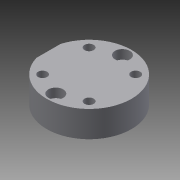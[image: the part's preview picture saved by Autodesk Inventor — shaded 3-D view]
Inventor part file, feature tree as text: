
AUTODESK INVENTOR PART (.ipt)
format: ipt  version: 2014 SP2 (Build 180246200, 246)  size: 247,296 bytes
history: native  units: in
note: dims shown in document units (in); Inventor stores cm internally (conversion verified against a paired STEP export)
features: other x259, sketch x7, hole x4, revolve x2, extrude x1, thread x1, pattern_linear x1
ambient origin geometry x8: Origin, YZ Plane, XZ Plane, XY Plane, X Axis, Y Axis, Z Axis, Center Point
bodies: Solid1 (feature_tree)
feature tree (275):
  revolve  "Revolution1"  [1 undecoded]
  extrude  "Extrusion1"  Depth=0.1831in TaperAngle=0.0deg
  revolve  "Revolution2"  [1 undecoded]
  thread  "Thread1"  [1 undecoded]
  hole  "Hole1"  [1 undecoded]
  hole  "Hole2"  [1 undecoded]
  hole  "Hole3"  [1 undecoded]
  hole  "Hole4"  [1 undecoded]
  pattern_linear  "Rectangular Pattern1"  [2 undecoded]
  other  "a1_XY"
  other  "a1_YZ"
  other  "a1_ZX"
  other  "a1_X"
  other  "a1_Y"
  other  "a1_Z"
  other  "a1_Center"
  other  "a2_XY"
  other  "a2_YZ"
  other  "a2_ZX"
  other  "a2_X"
  other  "a2_Y"
  other  "a2_Z"
  other  "a2_Center"
  other  "ar3_XY"
  other  "ar3_YZ"
  other  "ar3_ZX"
  other  "ar3_X"
  other  "ar3_Y"
  other  "ar3_Z"
  other  "ar3_Center"
  other  "ar4_XY"
  other  "ar4_YZ"
  other  "ar4_ZX"
  other  "ar4_X"
  other  "ar4_Y"
  other  "ar4_Z"
  other  "ar4_Center"
  other  "ar5_XY"
  other  "ar5_YZ"
  other  "ar5_ZX"
  other  "ar5_X"
  other  "ar5_Y"
  other  "ar5_Z"
  other  "ar5_Center"
  other  "ar6_XY"
  other  "ar6_YZ"
  other  "ar6_ZX"
  other  "ar6_X"
  other  "ar6_Y"
  other  "ar6_Z"
  other  "ar6_Center"
  other  "b1_XY"
  other  "b1_YZ"
  other  "b1_ZX"
  other  "b1_X"
  other  "b1_Y"
  other  "b1_Z"
  other  "b1_Center"
  other  "j_XY"
  other  "j_YZ"
  other  "j_ZX"
  other  "j_X"
  other  "j_Y"
  other  "j_Z"
  other  "j_Center"
  other  "k1_XY"
  other  "k1_YZ"
  other  "k1_ZX"
  other  "k1_X"
  other  "k1_Y"
  other  "k1_Z"
  other  "k1_Center"
  other  "k2_XY"
  other  "k2_YZ"
  other  "k2_ZX"
  other  "k2_X"
  other  "k2_Y"
  other  "k2_Z"
  other  "k2_Center"
  other  "l1_XY"
  other  "l1_YZ"
  other  "l1_ZX"
  other  "l1_X"
  other  "l1_Y"
  other  "l1_Z"
  other  "l1_Center"
  other  "l2_XY"
  other  "l2_YZ"
  other  "l2_ZX"
  other  "l2_X"
  other  "l2_Y"
  other  "l2_Z"
  other  "l2_Center"
  other  "po1_XY"
  other  "po1_YZ"
  other  "po1_ZX"
  other  "po1_X"
  other  "po1_Y"
  other  "po1_Z"
  other  "po1_Center"
  other  "po2_XY"
  other  "po2_YZ"
  other  "po2_ZX"
  other  "po2_X"
  other  "po2_Y"
  other  "po2_Z"
  other  "po2_Center"
  other  "po3_XY"
  other  "po3_YZ"
  other  "po3_ZX"
  other  "po3_X"
  other  "po3_Y"
  other  "po3_Z"
  other  "po3_Center"
  other  "r7_XY"
  other  "r7_YZ"
  other  "r7_ZX"
  other  "r7_X"
  other  "r7_Y"
  other  "r7_Z"
  other  "r7_Center"
  other  "r71_XY"
  other  "r71_YZ"
  other  "r71_ZX"
  other  "r71_X"
  other  "r71_Y"
  other  "r71_Z"
  other  "r71_Center"
  other  "r72_XY"
  other  "r72_YZ"
  other  "r72_ZX"
  other  "r72_X"
  other  "r72_Y"
  other  "r72_Z"
  other  "r72_Center"
  other  "r73_XY"
  other  "r73_YZ"
  other  "r73_ZX"
  other  "r73_X"
  other  "r73_Y"
  other  "r73_Z"
  other  "r73_Center"
  other  "rg_XY"
  other  "rg_YZ"
  other  "rg_ZX"
  other  "rg_X"
  other  "rg_Y"
  other  "rg_Z"
  other  "rg_Center"
  other  "rh_XY"
  other  "rh_YZ"
  other  "rh_ZX"
  other  "rh_X"
  other  "rh_Y"
  other  "rh_Z"
  other  "rh_Center"
  other  "rs_1_XY"
  other  "rs_1_YZ"
  other  "rs_1_ZX"
  other  "rs_1_X"
  other  "rs_1_Y"
  other  "rs_1_Z"
  other  "rs_1_Center"
  other  "rs_2_XY"
  other  "rs_2_YZ"
  other  "rs_2_ZX"
  other  "rs_2_X"
  other  "rs_2_Y"
  other  "rs_2_Z"
  other  "rs_2_Center"
  other  "rs_3_XY"
  other  "rs_3_YZ"
  other  "rs_3_ZX"
  other  "rs_3_X"
  other  "rs_3_Y"
  other  "rs_3_Z"
  other  "rs_3_Center"
  other  "rs_4_XY"
  other  "rs_4_YZ"
  other  "rs_4_ZX"
  other  "rs_4_X"
  other  "rs_4_Y"
  other  "rs_4_Z"
  other  "rs_4_Center"
  other  "sc1_XY"
  other  "sc1_YZ"
  other  "sc1_ZX"
  other  "sc1_X"
  other  "sc1_Y"
  other  "sc1_Z"
  other  "sc1_Center"
  other  "sc2_XY"
  other  "sc2_YZ"
  other  "sc2_ZX"
  other  "sc2_X"
  other  "sc2_Y"
  other  "sc2_Z"
  other  "sc2_Center"
  other  "sc3_XY"
  other  "sc3_YZ"
  other  "sc3_ZX"
  other  "sc3_X"
  other  "sc3_Y"
  other  "sc3_Z"
  other  "sc3_Center"
  other  "to_dummy_XY"
  other  "to_dummy_YZ"
  other  "to_dummy_ZX"
  other  "to_dummy_X"
  other  "to_dummy_Y"
  other  "to_dummy_Z"
  other  "to_dummy_Center"
  other  "to_nut_XY"
  other  "to_nut_YZ"
  other  "to_nut_ZX"
  other  "to_nut_X"
  other  "to_nut_Y"
  other  "to_nut_Z"
  other  "to_nut_Center"
  other  "to_rod_XY"
  other  "to_rod_YZ"
  other  "to_rod_ZX"
  other  "to_rod_X"
  other  "to_rod_Y"
  other  "to_rod_Z"
  other  "to_rod_Center"
  other  "to_tube_XY"
  other  "to_tube_YZ"
  other  "to_tube_ZX"
  other  "to_tube_X"
  other  "to_tube_Y"
  other  "to_tube_Z"
  other  "to_tube_Center"
  other  "to_wiper_XY"
  other  "to_wiper_YZ"
  other  "to_wiper_ZX"
  other  "to_wiper_X"
  other  "to_wiper_Y"
  other  "to_wiper_Z"
  other  "to_wiper_Center"
  other  "track1_XY"
  other  "track1_YZ"
  other  "track1_ZX"
  other  "track1_X"
  other  "track1_Y"
  other  "track1_Z"
  other  "track1_Center"
  other  "track2_XY"
  other  "track2_YZ"
  other  "track2_ZX"
  other  "track2_X"
  other  "track2_Y"
  other  "track2_Z"
  other  "track2_Center"
  other  "track3_XY"
  other  "track3_YZ"
  other  "track3_ZX"
  other  "track3_X"
  other  "track3_Y"
  other  "track3_Z"
  other  "track3_Center"
  other  "track4_XY"
  other  "track4_YZ"
  other  "track4_ZX"
  other  "track4_X"
  other  "track4_Y"
  other  "track4_Z"
  other  "track4_Center"
  sketch  "Sketch_1"  dims[d0=360.0deg d1=0.344in d2=0.0in]
  sketch  "Sketch_63"  dims[d40=0.0in d41=0.0in d42=0.0in d43=0.0in d44=0.0in d45=0.0in d46=0.0in d47=0.0in d48=0.0in d49=0.0in d50=0.0in d51=0.0in d52=0.0in d53=0.0in d54=0.0in d55=0.0in d56=0.0in d57=0.0in d58=0.0in d59=0.0in d60=0.0in]
  sketch  "Sketch_37"  dims[d27=0.0849in d28=0.344in d29=0.12in d30=0.1in d31=0.5635in d32=0.344in d33=0.0in d34=0.7874in d36=0.6109in d37=0.7874in d39=0.6109in]
  sketch  "Sketch4"  dims[d3=360.0deg d4=0.1831in d5=0.0in]
  sketch  "Sketch5"  dims[d6=0.61in d7=0.75in d8=0.375in d9=0.25in d10=0.5635in d11=0.1in d12=0.0in]
  sketch  "Sketch6"  dims[d13=0.1285in d14=0.75in d15=0.195in d16=0.12in d17=0.5635in d18=0.344in d19=0.0in]
  sketch  "Sketch7"  dims[d20=0.1285in d21=0.75in d22=0.195in d23=0.12in d24=0.5635in d25=0.344in d26=0.0in]
note: 9 required parameter values undecoded (feature->parameter linkage not recoverable at this tier; creation-order binding heuristic only, values carry confidence <= 0.55)